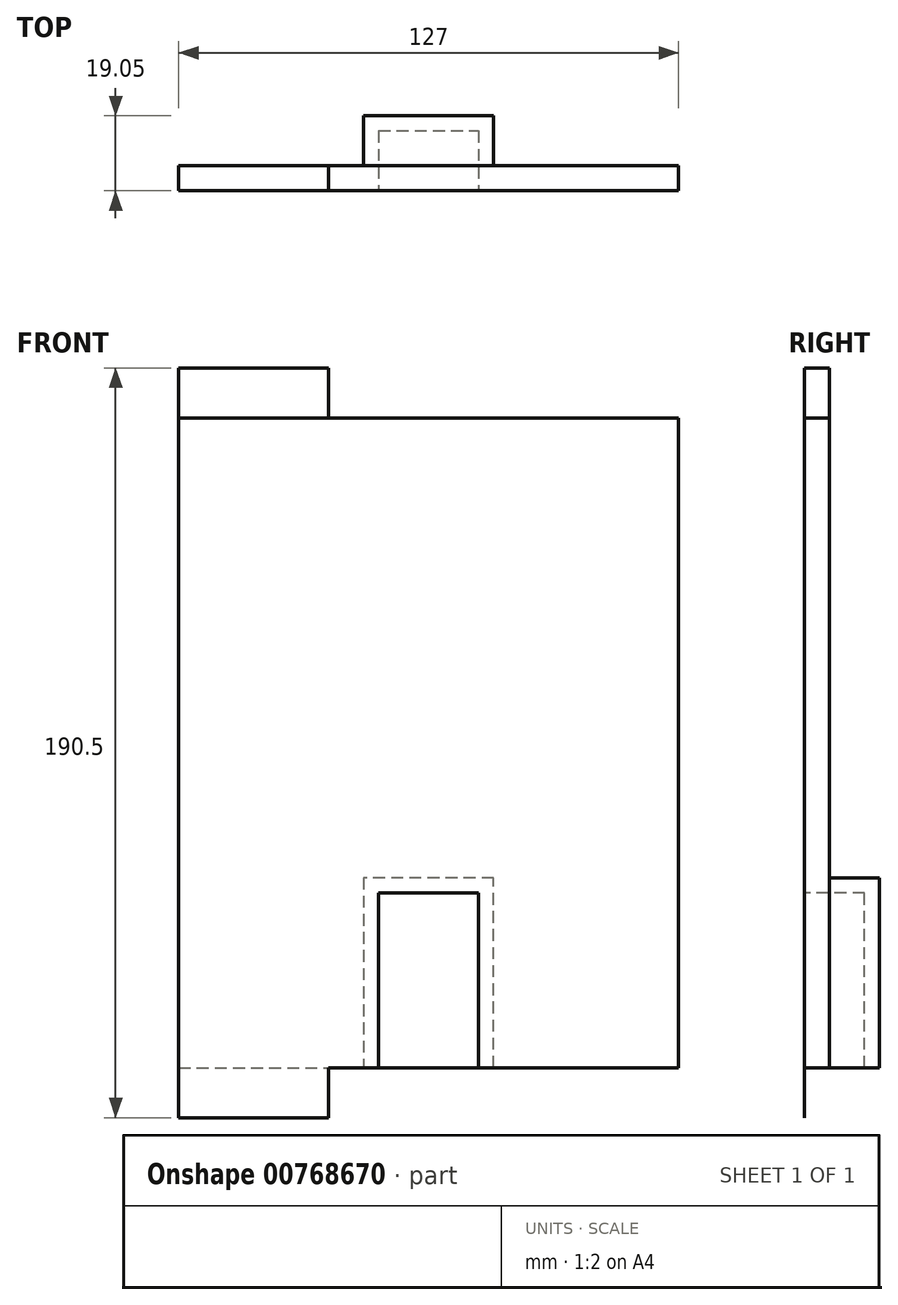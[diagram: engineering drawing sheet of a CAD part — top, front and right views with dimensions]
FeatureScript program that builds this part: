
annotation { "Feature Type Name" : "Feature", "Feature Type Description" : "" }
export const myFeature = defineFeature(function(context is Context, id is Id, definition is map)
    precondition{}
    {
        {
            var Q0;
            Q0=qCreatedBy(makeId("Front.planeOp"),FACE);
            var sketch = newSketch(context, id + "F0", { "sketchPlane" : qUnion([Q0])});
            skLineSegment(sketch, "E0.bottom", {"start": v(-52.81, 98.18) * mm, "end": v(74.19, 98.18) * mm});
            skLineSegment(sketch, "E0.top", {"start": v(-52.81, -66.92) * mm, "end": v(74.19, -66.92) * mm});
            skLineSegment(sketch, "E0.left", {"start": v(-52.81, 98.18) * mm, "end": v(-52.81, -66.92) * mm});
            skLineSegment(sketch, "E0.right", {"start": v(74.19, 98.18) * mm, "end": v(74.19, -66.92) * mm});
            skSolve(sketch);
        }
        {
            var Q0;
            Q0 = qSketchRegion(id + "F0", true);
            extrude(context, id + "F1", {"entities" : qUnion([Q0]), "depth" : 6.35 * mm, "offsetDistance" : 25.4 * mm});
        }
        {
            var Q0;
            Q0=makeQuery(id+"F1.opExtrude","CAP_FACE",FACE,{"disambiguationData":[OSD([sQuery(id+"F0.wireOp",EDGE,"E0.bottom"),sQuery(id+"F0.wireOp",EDGE,"E0.top"),sQuery(id+"F0.wireOp",EDGE,"E0.left"),sQuery(id+"F0.wireOp",EDGE,"E0.right")])],"isStart":false});
            var sketch = newSketch(context, id + "F2", { "sketchPlane" : qUnion([Q0])});
            skLineSegment(sketch, "E1", {"start": v(10.69, 98.18) * mm, "end": v(10.69, -66.92) * mm});
            skLineSegment(sketch, "E2", {"start": v(10.69, -66.92) * mm, "end": v(-2.01, -66.92) * mm});
            skLineSegment(sketch, "E3", {"start": v(-2.01, -66.92) * mm, "end": v(-2.01, -22.47) * mm});
            skLineSegment(sketch, "E4", {"start": v(-2.01, -22.47) * mm, "end": v(23.39, -22.47) * mm});
            skLineSegment(sketch, "E5", {"start": v(23.39, -22.47) * mm, "end": v(23.39, -66.92) * mm});
            skLineSegment(sketch, "E6", {"start": v(23.39, -66.92) * mm, "end": v(-2.01, -66.92) * mm});
            skLineSegment(sketch, "E7", {"start": v(27.2, -66.92) * mm, "end": v(27.2, -18.66) * mm});
            skLineSegment(sketch, "E8", {"start": v(27.2, -18.66) * mm, "end": v(-5.82, -18.66) * mm});
            skLineSegment(sketch, "E9", {"start": v(-5.82, -18.66) * mm, "end": v(-5.82, -66.92) * mm});
            skLineSegment(sketch, "E10", {"start": v(-5.82, -66.92) * mm, "end": v(-2.01, -66.92) * mm});
            skLineSegment(sketch, "E11", {"start": v(27.2, -66.92) * mm, "end": v(23.39, -66.92) * mm});
            skSolve(sketch);
        }
        {
            var Q0;
            {var subQ5=sQuery(id+"F2.wireOp",EDGE,"E3");Q0=makeQuery(id+"F2.imprint","IMPRINT",FACE,{"disambiguationData":[TD([[makeQuery(id+"F2.imprint","IMPRINT",EDGE,{"derivedFrom":subQ5}),-1.0]])]});}
            var Q1;
            {var subQ5=sQuery(id+"F2.wireOp",EDGE,"E5");Q1=makeQuery(id+"F2.imprint","IMPRINT",FACE,{"disambiguationData":[TD([[makeQuery(id+"F2.imprint","IMPRINT",EDGE,{"derivedFrom":subQ5}),-1.0]])]});}
            extrude(context, id + "F3", {"entities" : qUnion([Q0, Q1]), "operationType" : NewBodyOperationType.REMOVE, "oppositeDirection" : true, "depth" : 25.4 * mm, "offsetDistance" : 25.4 * mm});
        }
        {
            var Q0;
            {var subQ1=sQuery(id+"F2.wireOp",EDGE,"E3");Q0=makeQuery(id+"F2.imprint","IMPRINT",FACE,{"disambiguationData":[TD([[makeQuery(id+"F2.imprint","IMPRINT",EDGE,{"derivedFrom":subQ1}),1.0]])]});}
            var Q1;
            {var subQ1=sQuery(id+"F2.wireOp",EDGE,"E5");Q1=makeQuery(id+"F2.imprint","IMPRINT",FACE,{"disambiguationData":[TD([[makeQuery(id+"F2.imprint","IMPRINT",EDGE,{"derivedFrom":subQ1}),1.0]])]});}
            extrude(context, id + "F4", {"entities" : qUnion([Q0, Q1]), "operationType" : NewBodyOperationType.ADD, "oppositeDirection" : true, "depth" : 19.05 * mm, "offsetDistance" : 25.4 * mm});
        }
        {
            var Q0;
            {var subQ0=sQuery(id+"F2.wireOp",EDGE,"E4");Q0=makeQuery(id+"F4.boolean.opBoolean","MERGE",FACE,{"derivedFrom":[makeQuery(id+"F3.boolean.opBoolean","COPY",FACE,{"derivedFrom":makeQuery(id+"F3.opExtrude","SWEPT_FACE",FACE,{"disambiguationData":[OSD([subQ0])]})}),makeQuery(id+"F4.opExtrude","SWEPT_FACE",FACE,{"disambiguationData":[OSD([subQ0])]})]});}
            var sketch = newSketch(context, id + "F5", { "sketchPlane" : qUnion([Q0])});
            skLineSegment(sketch, "E12", {"start": v(-2.01, -8.9) * mm, "end": v(23.39, -8.9) * mm});
            skLineSegment(sketch, "E13", {"start": v(23.39, -8.9) * mm, "end": v(23.39, -12.7) * mm});
            skLineSegment(sketch, "E14", {"start": v(23.39, -12.7) * mm, "end": v(-2.01, -12.7) * mm});
            skLineSegment(sketch, "E15", {"start": v(-2.01, -12.7) * mm, "end": v(-2.01, -8.9) * mm});
            skSolve(sketch);
        }
        {
            var Q0;
            Q0=makeQuery(id+"F5.imprint","IMPRINT",FACE,{"disambiguationData":[TD([[makeQuery(id+"F5.imprint","IMPRINT",EDGE,{"derivedFrom":sQuery(id+"F5.wireOp",EDGE,"E12")}),-1.0]])]});
            extrude(context, id + "F6", {"entities" : qUnion([Q0]), "operationType" : NewBodyOperationType.ADD, "depth" : 44.45 * mm, "offsetDistance" : 25.4 * mm});
        }
        {
            var Q0;
            Q0=makeQuery(id+"F1.opExtrude","CAP_FACE",FACE,{"disambiguationData":[OSD([sQuery(id+"F0.wireOp",EDGE,"E0.bottom"),sQuery(id+"F0.wireOp",EDGE,"E0.top"),sQuery(id+"F0.wireOp",EDGE,"E0.left"),sQuery(id+"F0.wireOp",EDGE,"E0.right")])],"isStart":false});
            var sketch = newSketch(context, id + "F7", { "sketchPlane" : qUnion([Q0])});
            skLineSegment(sketch, "E16.bottom", {"start": v(-52.81, 98.18) * mm, "end": v(-14.71, 98.18) * mm});
            skLineSegment(sketch, "E16.top", {"start": v(-52.81, 110.88) * mm, "end": v(-14.71, 110.88) * mm});
            skLineSegment(sketch, "E16.left", {"start": v(-52.81, 98.18) * mm, "end": v(-52.81, 110.88) * mm});
            skLineSegment(sketch, "E16.right", {"start": v(-14.71, 98.18) * mm, "end": v(-14.71, 110.88) * mm});
            skSolve(sketch);
        }
        {
            var Q0;
            Q0 = qSketchRegion(id + "F7", true);
            extrude(context, id + "F8", {"entities" : qUnion([Q0]), "oppositeDirection" : true, "depth" : 6.35 * mm, "offsetDistance" : 25.4 * mm});
        }
        {
            var Q0;
            Q0=makeQuery(id+"F1.opExtrude","CAP_FACE",FACE,{"disambiguationData":[OSD([sQuery(id+"F0.wireOp",EDGE,"E0.bottom"),sQuery(id+"F0.wireOp",EDGE,"E0.top"),sQuery(id+"F0.wireOp",EDGE,"E0.left"),sQuery(id+"F0.wireOp",EDGE,"E0.right")])],"isStart":false});
            var sketch = newSketch(context, id + "F9", { "sketchPlane" : qUnion([Q0])});
            skLineSegment(sketch, "E17.bottom", {"start": v(-52.81, 106.2) * mm, "end": v(-14.71, 106.2) * mm});
            skLineSegment(sketch, "E17.top", {"start": v(-52.81, 115.1) * mm, "end": v(-14.71, 115.1) * mm});
            skLineSegment(sketch, "E17.left", {"start": v(-52.81, 106.2) * mm, "end": v(-52.81, 115.1) * mm});
            skLineSegment(sketch, "E17.right", {"start": v(-14.71, 106.2) * mm, "end": v(-14.71, 115.1) * mm});
            skSolve(sketch);
        }
        {
            var Q0;
            Q0 = qSketchRegion(id + "F9", true);
            extrude(context, id + "F10", {"entities" : qUnion([Q0]), "depth" : 2.54 * mm, "offsetDistance" : 25.4 * mm});
        }
        {
            var Q0;
            Q0=makeQuery(id+"F1.opExtrude","CAP_FACE",FACE,{"disambiguationData":[OSD([sQuery(id+"F0.wireOp",EDGE,"E0.bottom"),sQuery(id+"F0.wireOp",EDGE,"E0.top"),sQuery(id+"F0.wireOp",EDGE,"E0.left"),sQuery(id+"F0.wireOp",EDGE,"E0.right")])],"isStart":false});
            var sketch = newSketch(context, id + "F11", { "sketchPlane" : qUnion([Q0])});
            skLineSegment(sketch, "E18.bottom", {"start": v(-52.81, -66.92) * mm, "end": v(-14.71, -66.92) * mm});
            skLineSegment(sketch, "E18.top", {"start": v(-52.81, -79.62) * mm, "end": v(-14.71, -79.62) * mm});
            skLineSegment(sketch, "E18.left", {"start": v(-52.81, -66.92) * mm, "end": v(-52.81, -79.62) * mm});
            skLineSegment(sketch, "E18.right", {"start": v(-14.71, -66.92) * mm, "end": v(-14.71, -79.62) * mm});
            skSolve(sketch);
        }
        {
            var Q0;
            Q0=makeQuery(id+"F11.imprint","IMPRINT",FACE,{"disambiguationData":[TD([[makeQuery(id+"F11.imprint","IMPRINT",EDGE,{"derivedFrom":sQuery(id+"F11.wireOp",EDGE,"E18.bottom")}),-1.0]])]});
            extrude(context, id + "F12", {"entities" : qUnion([Q0]), "operationType" : NewBodyOperationType.ADD, "oppositeDirection" : true, "depth" : 1 / 101.6 * mm, "offsetDistance" : 25.4 * mm});
        }
        {
            var Q0;
            Q0=makeQuery(id+"F10.opExtrude","SWEPT_BODY",BODY,{"disambiguationData":[OSD([sQuery(id+"F9.wireOp",EDGE,"E17.bottom"),sQuery(id+"F9.wireOp",EDGE,"E17.top"),sQuery(id+"F9.wireOp",EDGE,"E17.left"),sQuery(id+"F9.wireOp",EDGE,"E17.right")])]});
            deleteBodies(context, id + "F13", {"entities" : qUnion([Q0])});
        }
    });
